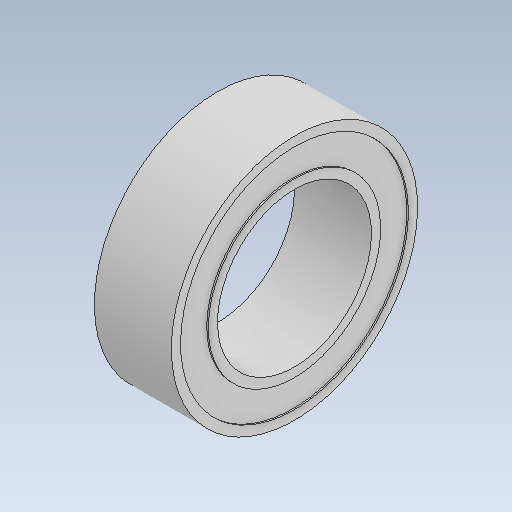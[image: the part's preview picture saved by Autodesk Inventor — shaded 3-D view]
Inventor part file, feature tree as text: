
AUTODESK INVENTOR PART (.ipt)
format: ipt  version: 2020 (Build 240168000, 168)  size: 139,776 bytes
history: native  units: mm
features: extrude x2, other x1, sketch x1
ambient origin geometry x8: Origin, YZ Plane, XZ Plane, XY Plane, X Axis, Y Axis, Z Axis, Center Point
bodies: Body1 (feature_tree)
feature tree (4):
  other  "Твердое тело1"
  sketch  "Эскиз1"
  extrude  "Выдавливание1"  Depth=5.0mm
  extrude  "Выдавливание2"  Depth=8.0mm
